# Revit family: Furniture-Console_Table_Legs-KOHLER-Farmstead-K-21105_1
name_source: partatom
category: Specialty Equipment
units: mm (PartAtom-declared; Revit-internal decimal feet)

## family parameters
Cut with Voids When Loaded = No
Host = Face
OmniClass Number = 23.31.25.00
OmniClass Title = Toilet and Bath Specialties
Part Type = Normal
Room Calculation Point = No
Round Connector Dimension = Use Diameter
Shared = No

## types (4) — shared parameters
ADA Compliant = No
Assembly Code = E20
Date Modified = 05/24/2023
Default Elevation = 0"
Description = Transitional legs
Height = 26 1/8"
Length = 4 1/4"
Manufacturer = Kohler Co.
Master Format 2014 = 06 41 93
Master Format 2014 Name = Cabinet and Drawer Hardware
Material = Enameled Cast Iron
Product Documentation Link = https://www.us.kohler.com
Product Name = Farmstead
Product Page URL = http://www.us.kohler.com
URL = https://www.us.kohler.com
WaterSense Certified = No

## per-type parameters (varying)
| type | Finish | Model | Type |
| 0-White | KOHLER-Enameled_Cast_Iron-0-White | K-21105-0 | 1 |
| P5-Iron Black | KOHLER-Enameled_Cast_Iron-P5-Iron_Black | K-21105-P5 | 2 |
| V10-Peachblow | KOHLER-Enameled_Cast_Iron-V10-Peachblow | K-21105-V10 | 3 |
| H15-Spring Green | KOHLER-Enameled_Cast_Iron-H15-Spring_Green | K-21105-H15 | 4 |

## geometry (parser evidence)
native form markers: Sweep x5
no freeform markers — native parametric forms only
